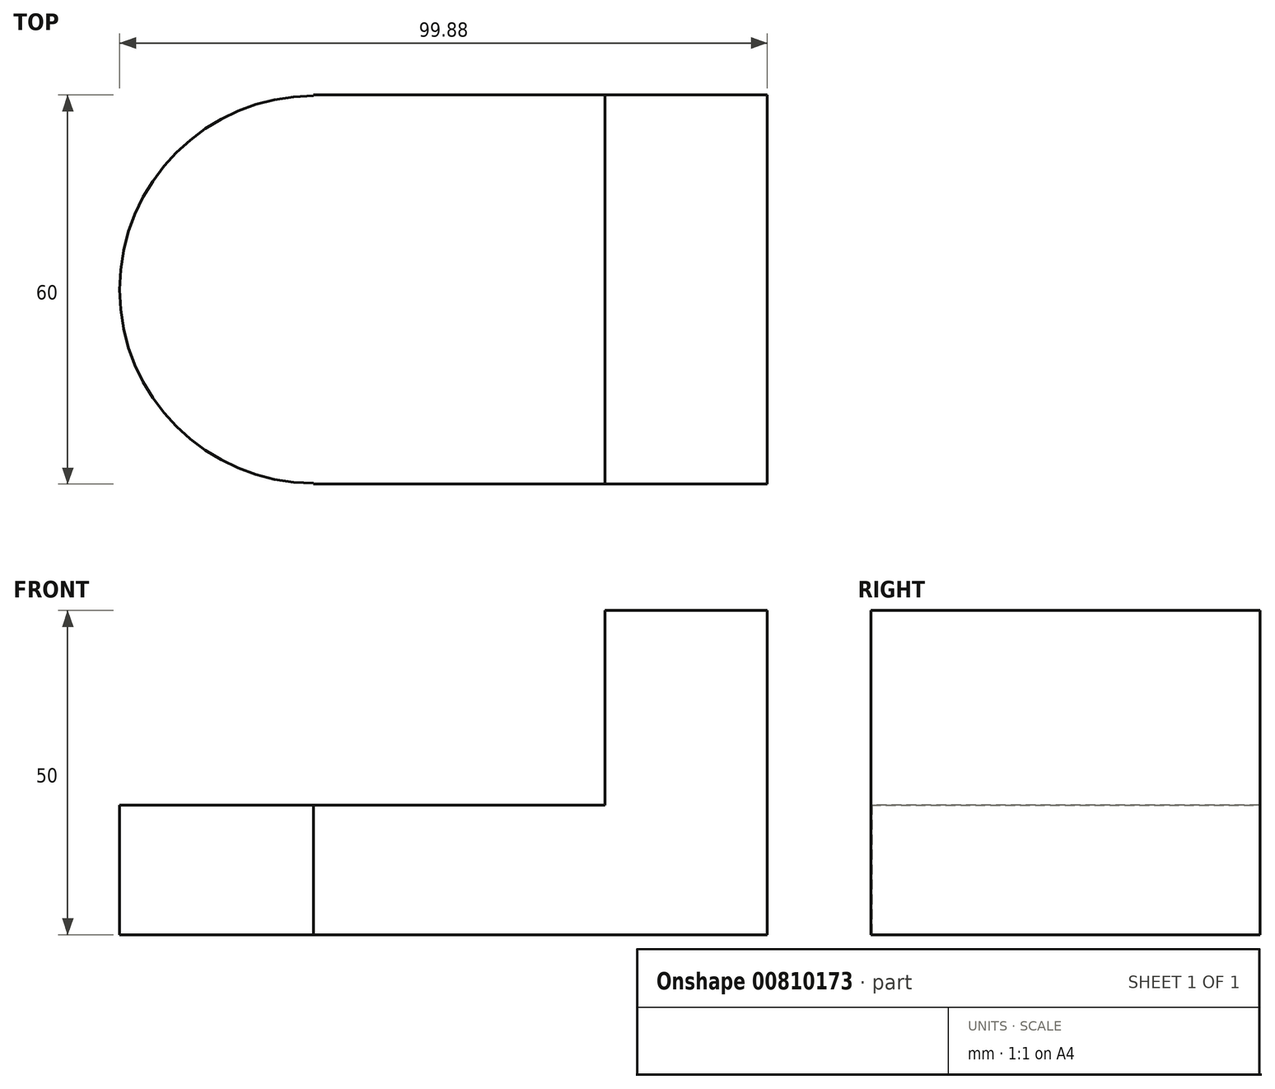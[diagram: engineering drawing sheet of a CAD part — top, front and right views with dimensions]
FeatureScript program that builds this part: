
annotation { "Feature Type Name" : "Feature", "Feature Type Description" : "" }
export const myFeature = defineFeature(function(context is Context, id is Id, definition is map)
    precondition{}
    {
        {
            var Q0;
            Q0=qCreatedBy(makeId("Top.planeOp"),FACE);
            var sketch = newSketch(context, id + "F0", { "sketchPlane" : qUnion([Q0])});
            skLineSegment(sketch, "E0.bottom", {"start": v(-70, 0) * mm, "end": v(0, 0) * mm});
            skLineSegment(sketch, "E0.top", {"start": v(-70, -60) * mm, "end": v(0, -60) * mm});
            skLineSegment(sketch, "E0.left", {"start": v(-70, 0) * mm, "end": v(-70, -0.12) * mm});
            skLineSegment(sketch, "E0.right", {"start": v(0, 0) * mm, "end": v(0, -60) * mm});
            skArc(sketch, "E1", {"start": v(-70, -0.12) * mm, "mid": v(-99.88, -30) * mm, "end": v(-70, -59.88) * mm});
            skLineSegment(sketch, "E2.trimOffspring", {"start": v(-70, -59.88) * mm, "end": v(-70, -60) * mm});
            skSolve(sketch);
        }
        {
            var Q0;
            Q0=makeQuery(id+"F0.imprint","IMPRINT",FACE,{"disambiguationData":[TD([[makeQuery(id+"F0.imprint","IMPRINT",EDGE,{"derivedFrom":sQuery(id+"F0.wireOp",EDGE,"E0.bottom")}),-1.0]])]});
            extrude(context, id + "F1", {"entities" : qUnion([Q0]), "depth" : 20 * mm, "offsetDistance" : 25 * mm});
        }
        {
            var Q0;
            Q0=makeQuery(id+"F1.opExtrude","CAP_FACE",FACE,{"disambiguationData":[OSD([sQuery(id+"F0.wireOp",EDGE,"E0.bottom"),sQuery(id+"F0.wireOp",EDGE,"E0.top"),sQuery(id+"F0.wireOp",EDGE,"E0.left"),sQuery(id+"F0.wireOp",EDGE,"E0.right"),sQuery(id+"F0.wireOp",EDGE,"E1"),sQuery(id+"F0.wireOp",EDGE,"E2.trimOffspring")])],"isStart":false});
            var sketch = newSketch(context, id + "F2", { "sketchPlane" : qUnion([Q0])});
            skLineSegment(sketch, "E3.bottom", {"start": v(-25, 0) * mm, "end": v(0, 0) * mm});
            skLineSegment(sketch, "E3.top", {"start": v(-25, 0) * mm, "end": v(0, 0) * mm});
            skLineSegment(sketch, "E3.left", {"start": v(-25, 0) * mm, "end": v(-25, 0) * mm});
            skLineSegment(sketch, "E3.right", {"start": v(0, 0) * mm, "end": v(0, 0) * mm});
            skLineSegment(sketch, "E4.bottom", {"start": v(0, -60) * mm, "end": v(-25, -60) * mm});
            skLineSegment(sketch, "E4.top", {"start": v(0, 0) * mm, "end": v(-25, 0) * mm});
            skLineSegment(sketch, "E4.left", {"start": v(0, -60) * mm, "end": v(0, 0) * mm});
            skLineSegment(sketch, "E4.right", {"start": v(-25, -60) * mm, "end": v(-25, 0) * mm});
            skSolve(sketch);
        }
        {
            var Q0;
            Q0=makeQuery(id+"F2.imprint","IMPRINT",FACE,{"disambiguationData":[TD([[makeQuery(id+"F2.imprint","IMPRINT",EDGE,{"derivedFrom":sQuery(id+"F2.wireOp",EDGE,"E4.bottom")}),1.0]])]});
            extrude(context, id + "F3", {"entities" : qUnion([Q0]), "operationType" : NewBodyOperationType.ADD, "depth" : 30 * mm, "offsetDistance" : 25 * mm});
        }
    });
